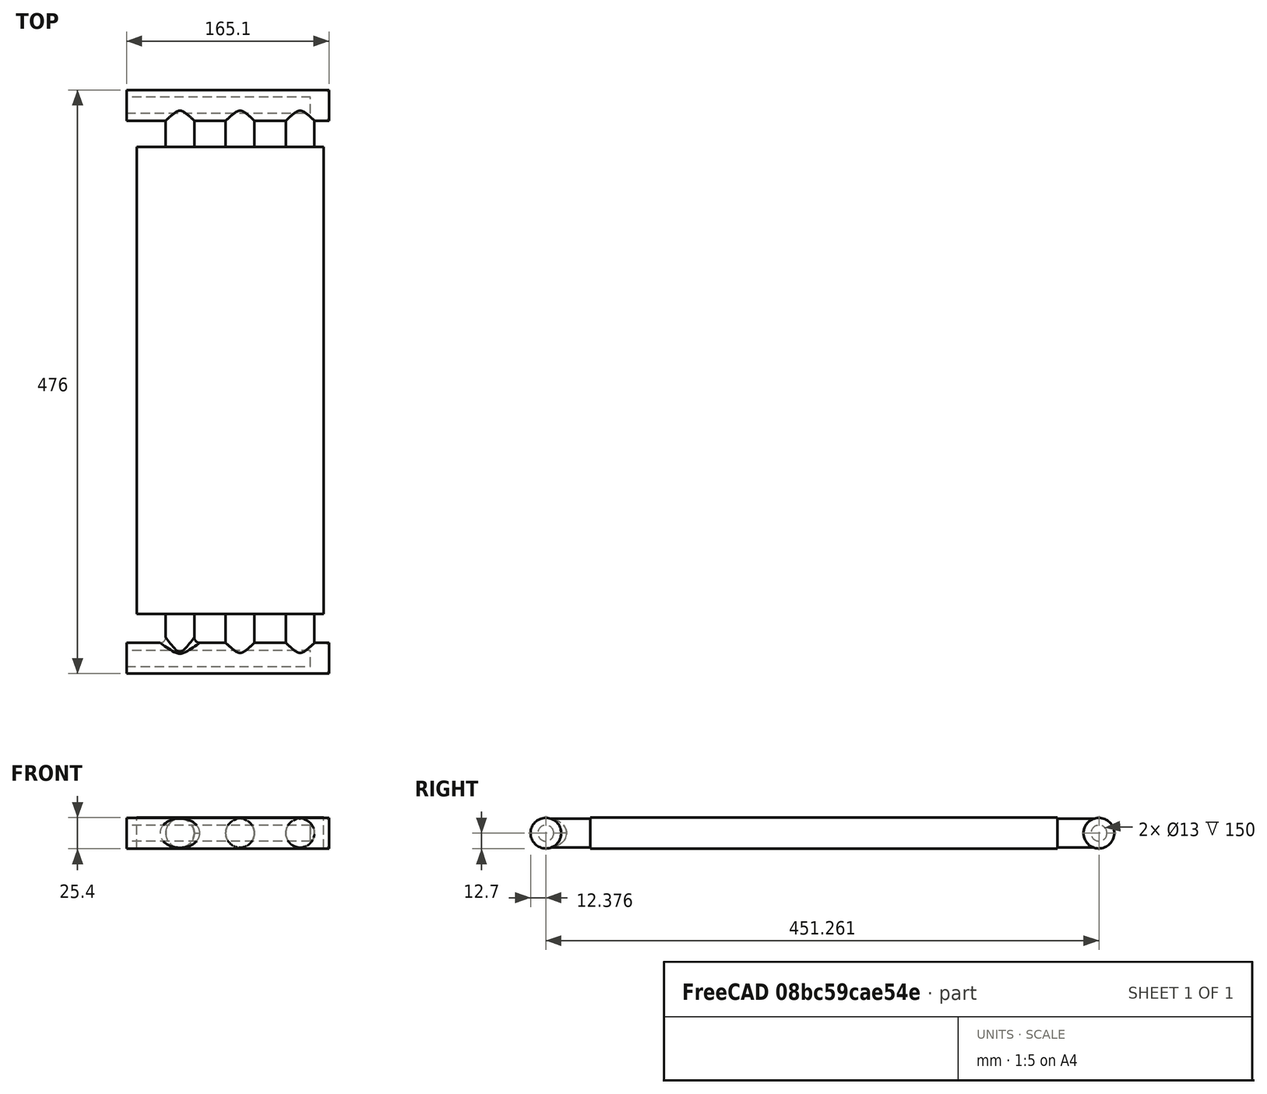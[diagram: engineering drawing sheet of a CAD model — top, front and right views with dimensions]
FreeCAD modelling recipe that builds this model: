
FCSTD DOCUMENT  (FreeCAD 0.16R6706 (Git))
Label: PC_1240_cooler
License: All rights reserved
LicenseURL: http://en.wikipedia.org/wiki/All_rights_reserved
objects: Part::Cylinder×5, Part::MultiFuse×2, PartDesign::Fillet×2, Part::Box×1, Sketcher::SketchObject×1, PartDesign::Pocket×1
note: 13 computed .brp shape members not serialized (recipe doc carries the construction recipe); baked Part::Feature solids carry a one-line shape summary decoded from their .brp

FEATURE [Part::Cylinder] cylinder
  Angle = 360
  Height = 165.1
  Placement = pos=(-92.55,-10,0) rot=(0,1,0;1.5708rad)
  Radius = 12.5
FEATURE [Part::Cylinder] cylinder001
  Angle = 360
  Height = 165.1
  Placement = pos=(-92.55,441,0) rot=(0,1,0;1.5708rad)
  Radius = 12.5
FEATURE [Part::Cylinder] cylinder002
  Angle = 360
  Height = 452.12
  Placement = pos=(-49,442.81,0) rot=(1,0,0;1.5708rad)
  Radius = 11.7
FEATURE [Part::Cylinder] cylinder003
  Angle = 360
  Height = 452.12
  Placement = pos=(0,442.81,0) rot=(1,0,0;1.5708rad)
  Radius = 11.7
FEATURE [Part::Cylinder] cylinder004
  Angle = 360
  Height = 452.12
  Placement = pos=(49,442.81,0) rot=(1,0,0;1.5708rad)
  Radius = 11.7
FEATURE [Part::Box] cube
  Height = 25.4
  Length = 152.4
  Placement = pos=(-84.2,26.25,-12.7) rot=(0,0,1;0rad)
  Width = 381
FEATURE [Part::MultiFuse] Fusion
  Shapes = -> [cylinder,cylinder001,cylinder002,cylinder004,cylinder003]
FEATURE [Part::MultiFuse] Fusion001
  Shapes = -> [cube,Fusion]
FEATURE [PartDesign::Fillet] Fillet
  Base = -> Fusion001 [Edge44,Edge30]
  Radius = 4.5
FEATURE [Sketcher::SketchObject] Sketch
  Placement = pos=(-92.55,0,0) rot=(0.57735,-0.57735,-0.57735;2.0944rad)
  Support = -> Fillet [Face18]
  sketch-geometry (2):
    g0: Circle CenterX=10.1241 CenterY=0 CenterZ=0 NormalX=0 NormalY=0 NormalZ=1 Radius=6.5
    g1: Circle CenterX=-441.137 CenterY=0 CenterZ=0 NormalX=0 NormalY=0 NormalZ=1 Radius=6.5
  constraints (3):
    c: PointOnObject(g0,g-1)
    c: Radius(g0) = 6.5
    c: Radius(g1) = 6.5
FEATURE [PartDesign::Pocket] Pocket
  Length = 150
  Sketch = -> Sketch
  Type = 0
FEATURE [PartDesign::Fillet] Fillet001
  Base = -> Pocket [Edge14,Edge56]
  Radius = 3.5
